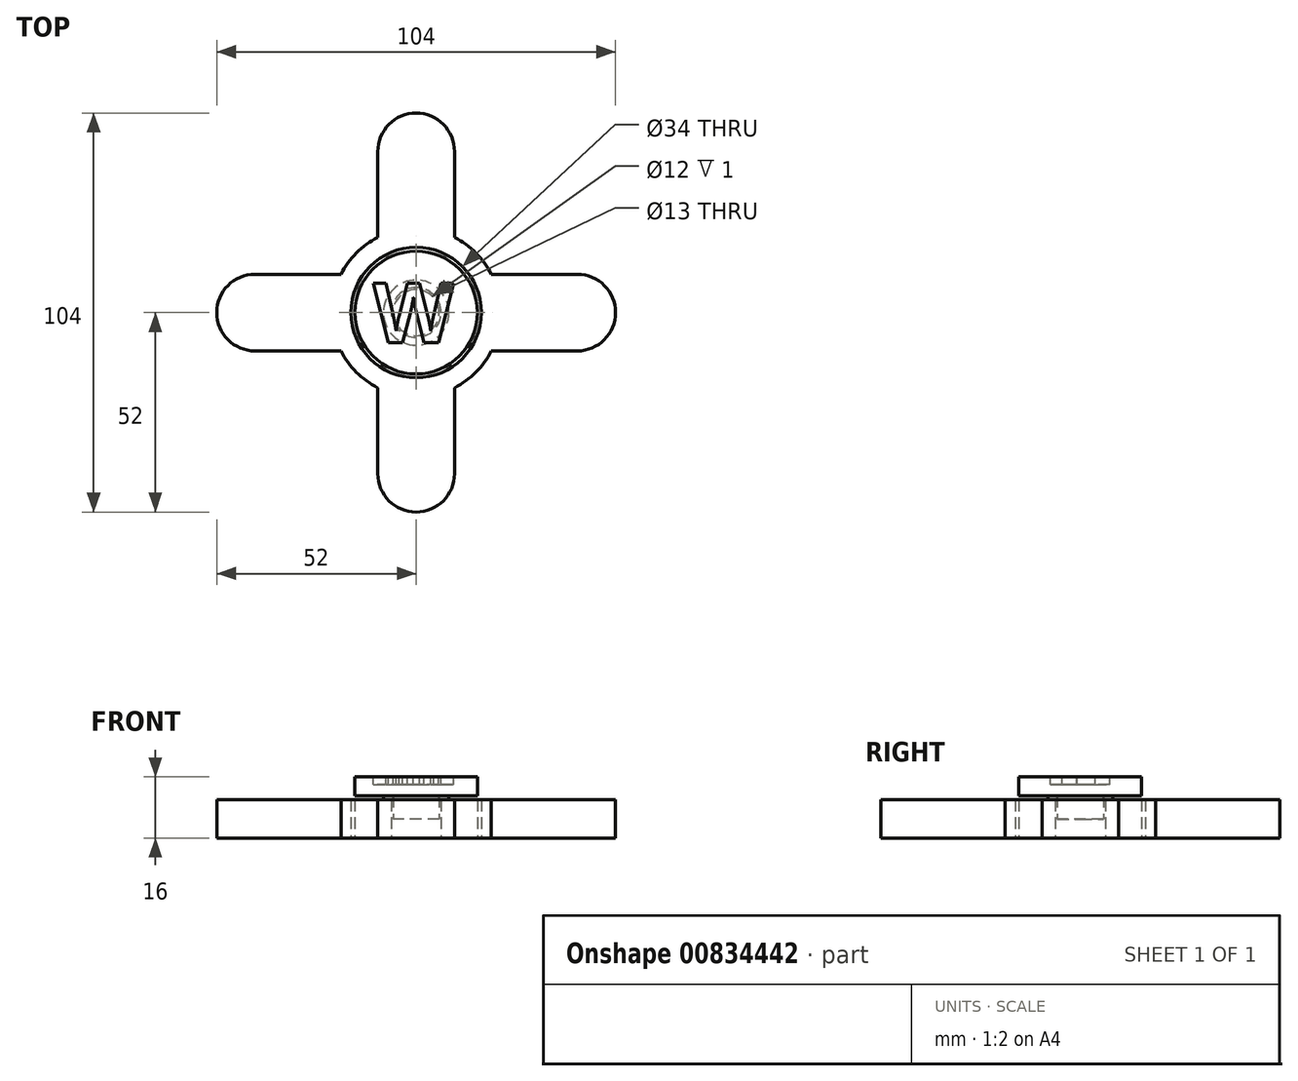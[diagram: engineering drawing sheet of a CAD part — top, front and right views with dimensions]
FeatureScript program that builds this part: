
annotation { "Feature Type Name" : "Feature", "Feature Type Description" : "" }
export const myFeature = defineFeature(function(context is Context, id is Id, definition is map)
    precondition{}
    {
        {
            var Q0;
            Q0=qCreatedBy(makeId("Top.planeOp"),FACE);
            var sketch = newSketch(context, id + "F0", { "sketchPlane" : qUnion([Q0])});
            skCircle(sketch, "E0", {"center": v(0, 0) * mm, "radius": 16 * mm});
            skCircle(sketch, "E1", {"center": v(0, 0) * mm, "radius": 6.5 * mm});
            skCircle(sketch, "E2", {"center": v(0, 0) * mm, "radius": 17 * mm});
            skCircle(sketch, "E3", {"center": v(0, 0) * mm, "radius": 22 * mm});
            skCircle(sketch, "E4", {"center": v(0, 0) * mm, "radius": 4.5 * mm});
            skPoint(sketch, "E5", {"position": v(0, -22) * mm});
            skLineSegment(sketch, "E6", {"start": v(-10, -19.6) * mm, "end": v(-10, -52) * mm});
            skLineSegment(sketch, "E7", {"start": v(-10, -52) * mm, "end": v(10, -52) * mm});
            skLineSegment(sketch, "E8", {"start": v(10, -52) * mm, "end": v(10, -19.6) * mm});
            skPoint(sketch, "E9", {"position": v(0, -52) * mm});
            skPoint(sketch, "E10", {"position": v(-22, 0) * mm});
            skPoint(sketch, "E11", {"position": v(22, 0) * mm});
            skPoint(sketch, "E12", {"position": v(0, 22) * mm});
            skLineSegment(sketch, "E13", {"start": v(-19.6, 10) * mm, "end": v(-52, 10) * mm});
            skLineSegment(sketch, "E14", {"start": v(-52, 10) * mm, "end": v(-52, -10) * mm});
            skLineSegment(sketch, "E15", {"start": v(-52, -10) * mm, "end": v(-19.6, -10) * mm});
            skPoint(sketch, "E16", {"position": v(-52, 0) * mm});
            skLineSegment(sketch, "E17", {"start": v(-10, 19.6) * mm, "end": v(-10, 52) * mm});
            skLineSegment(sketch, "E18", {"start": v(-10, 52) * mm, "end": v(10, 52) * mm});
            skLineSegment(sketch, "E19", {"start": v(10, 52) * mm, "end": v(10, 19.6) * mm});
            skPoint(sketch, "E20", {"position": v(0, 52) * mm});
            skLineSegment(sketch, "E21", {"start": v(19.6, -10) * mm, "end": v(52, -10) * mm});
            skLineSegment(sketch, "E22", {"start": v(52, -10) * mm, "end": v(52, 10) * mm});
            skLineSegment(sketch, "E23", {"start": v(52, 10) * mm, "end": v(19.6, 10) * mm});
            skPoint(sketch, "E24", {"position": v(52, 0) * mm});
            skSolve(sketch);
        }
        {
            var Q0;
            {var subQ0=sQuery(id+"F0.wireOp",EDGE,"gpfM4k37-eCNT-VDhr-O2bJ-2ocuH3XYZRLL");var subQ1=sQuery(id+"F0.wireOp",EDGE,"E2");var subQ2=makeQuery(id+"F0.imprint","INTERSECT",VERTEX,{"derivedFrom":[subQ1,subQ0]});Q0=makeQuery(id+"F0.imprint","IMPRINT",FACE,{"disambiguationData":[TD([[makeQuery(id+"F0.imprint","IMPRINT",EDGE,{"disambiguationData":[TD([[subQ2,1.0]])],"derivedFrom":subQ1}),-1.0]])]});}
            var Q1;
            {var subQ0=sQuery(id+"F0.wireOp",EDGE,"wSeqBDBI-Kv3G-UAp7-a8cB-W62R1kd8twcA");var subQ1=sQuery(id+"F0.wireOp",EDGE,"E2");var subQ2=makeQuery(id+"F0.imprint","INTERSECT",VERTEX,{"derivedFrom":[subQ1,subQ0]});Q1=makeQuery(id+"F0.imprint","IMPRINT",FACE,{"disambiguationData":[TD([[makeQuery(id+"F0.imprint","IMPRINT",EDGE,{"disambiguationData":[TD([[subQ2,1.0]])],"derivedFrom":subQ1}),-1.0]])]});}
            var Q2;
            {var subQ0=sQuery(id+"F0.wireOp",EDGE,"S2Hn9LyL-7IjH-aa6G-lDFo-Ye3rjhQq9e6S");var subQ1=sQuery(id+"F0.wireOp",EDGE,"E2");var subQ2=makeQuery(id+"F0.imprint","INTERSECT",VERTEX,{"derivedFrom":[subQ1,subQ0]});Q2=makeQuery(id+"F0.imprint","IMPRINT",FACE,{"disambiguationData":[TD([[makeQuery(id+"F0.imprint","IMPRINT",EDGE,{"disambiguationData":[TD([[subQ2,-1.0]])],"derivedFrom":subQ1}),-1.0]])]});}
            var Q3;
            Q3=makeQuery(id+"F0.imprint","IMPRINT",FACE,{"disambiguationData":[TD([[makeQuery(id+"F0.imprint","IMPRINT",EDGE,{"derivedFrom":sQuery(id+"F0.wireOp",EDGE,"E0")}),1.0]])]});
            var Q4;
            Q4=makeQuery(id+"F0.imprint","IMPRINT",FACE,{"disambiguationData":[TD([[makeQuery(id+"F0.imprint","IMPRINT",EDGE,{"derivedFrom":sQuery(id+"F0.wireOp",EDGE,"E3")}),-1.0]])]});
            extrude(context, id + "F1", {"entities" : qUnion([Q0, Q1, Q2, Q3, Q4]), "depth" : 10 * mm, "offsetDistance" : 25 * mm});
        }
        {
            var Q0;
            Q0=qCreatedBy(makeId("Top.planeOp"),FACE);
            cPlane(context, id + "F2", {"entities" : qUnion([Q0]), "cplaneType" : CPlaneType.OFFSET, "offset" : 5 * mm, "width" : 150 * mm, "height" : 150 * mm});
        }
        {
            var Q0;
            Q0=qCreatedBy(id+"F2.planeOp",FACE);
            var sketch = newSketch(context, id + "F3", { "sketchPlane" : qUnion([Q0])});
            skCircle(sketch, "E25.0", {"center": v(0, 0) * mm, "radius": 16 * mm});
            skCircle(sketch, "E26.0", {"center": v(0, 0) * mm, "radius": 17 * mm});
            skCircle(sketch, "E27.0", {"center": v(0, 0) * mm, "radius": 22 * mm});
            skCircle(sketch, "E28.0", {"center": v(0, 0) * mm, "radius": 6.5 * mm});
            skCircle(sketch, "E29", {"center": v(0, 0) * mm, "radius": 6 * mm});
            skSolve(sketch);
        }
        {
            var Q0;
            Q0=makeQuery(id+"F3.imprint","IMPRINT",FACE,{"disambiguationData":[TD([[makeQuery(id+"F3.imprint","IMPRINT",EDGE,{"derivedFrom":sQuery(id+"F3.wireOp",EDGE,"E29")}),1.0]])]});
            extrude(context, id + "F4", {"entities" : qUnion([Q0]), "depth" : 6 * mm, "offsetDistance" : 25 * mm});
        }
        {
            var Q0;
            Q0=makeQuery(id+"F4.opExtrude","CAP_FACE",FACE,{"disambiguationData":[OSD([sQuery(id+"F3.wireOp",EDGE,"E29")])],"isStart":false});
            var sketch = newSketch(context, id + "F5", { "sketchPlane" : qUnion([Q0])});
            skCircle(sketch, "E30.0", {"center": v(0, 0) * mm, "radius": 16 * mm});
            skSolve(sketch);
        }
        {
            var Q0;
            Q0=makeQuery(id+"F5.imprint","IMPRINT",FACE,{"disambiguationData":[TD([[makeQuery(id+"F5.imprint","IMPRINT",EDGE,{"derivedFrom":sQuery(id+"F5.wireOp",EDGE,"E30.0")}),1.0]])]});
            var Q1;
            Q1=makeQuery(id+"F5.imprint","IMPRINT",FACE,{"disambiguationData":[TD([[makeQuery(id+"F5.imprint","IMPRINT",EDGE,{"derivedFrom":makeQuery(id+"F4.opExtrude","CAP_EDGE",EDGE,{"disambiguationData":[OSD([sQuery(id+"F3.wireOp",EDGE,"E29")])],"isStart":false})}),1.0]])]});
            extrude(context, id + "F6", {"entities" : qUnion([Q0, Q1]), "depth" : 5 * mm, "offsetDistance" : 25 * mm});
        }
        {
            var Q0;
            Q0=makeQuery(id+"F6.opExtrude","CAP_FACE",FACE,{"disambiguationData":[OSD([sQuery(id+"F5.wireOp",EDGE,"E30.0")])],"isStart":false});
            var sketch = newSketch(context, id + "F7", { "sketchPlane" : qUnion([Q0])});
            skPoint(sketch, "E31", {"position": v(0, 0) * mm});
            skCircle(sketch, "E32.0", {"center": v(0, 0) * mm, "radius": 16 * mm});
            skPoint(sketch, "E33", {"position": v(16, 0) * mm});
            skText(sketch, "E34", { "text": "W", "fontName": "OpenSans-Bold.ttf"});
            const initialGuessF7  = {"E34": [-0.01114, -0.00778, 1, 0, 0.01555]};
            skSetInitialGuess(sketch, initialGuessF7);
            skSolve(sketch);
        }
        {
            var Q0;
            Q0=makeQuery(id+"F7.imprint","IMPRINT",FACE,{"disambiguationData":[TD([[makeQuery(id+"F7.imprint","IMPRINT",EDGE,{"derivedFrom":sQuery(id+"F7.wireOp",EDGE,"E34.sketch_text.stroke-0")}),-1.0]])]});
            extrude(context, id + "F8", {"entities" : qUnion([Q0]), "operationType" : NewBodyOperationType.REMOVE, "oppositeDirection" : true, "depth" : 2 * mm, "offsetDistance" : 25 * mm});
        }
        {
            var Q0;
            Q0=makeQuery(id+"F1.opExtrude","SWEPT_EDGE",EDGE,{"disambiguationData":[OSD([sQuery(id+"F0.wireOp",EDGE,"E14"),sQuery(id+"F0.wireOp",EDGE,"E15")])]});
            var Q1;
            Q1=makeQuery(id+"F1.opExtrude","SWEPT_EDGE",EDGE,{"disambiguationData":[OSD([sQuery(id+"F0.wireOp",EDGE,"E13"),sQuery(id+"F0.wireOp",EDGE,"E14")])]});
            var Q2;
            Q2=makeQuery(id+"F1.opExtrude","SWEPT_EDGE",EDGE,{"disambiguationData":[OSD([sQuery(id+"F0.wireOp",EDGE,"E17"),sQuery(id+"F0.wireOp",EDGE,"E18")])]});
            var Q3;
            Q3=makeQuery(id+"F1.opExtrude","SWEPT_EDGE",EDGE,{"disambiguationData":[OSD([sQuery(id+"F0.wireOp",EDGE,"E18"),sQuery(id+"F0.wireOp",EDGE,"E19")])]});
            var Q4;
            Q4=makeQuery(id+"F1.opExtrude","SWEPT_EDGE",EDGE,{"disambiguationData":[OSD([sQuery(id+"F0.wireOp",EDGE,"E22"),sQuery(id+"F0.wireOp",EDGE,"E23")])]});
            var Q5;
            Q5=makeQuery(id+"F1.opExtrude","SWEPT_EDGE",EDGE,{"disambiguationData":[OSD([sQuery(id+"F0.wireOp",EDGE,"E21"),sQuery(id+"F0.wireOp",EDGE,"E22")])]});
            var Q6;
            Q6=makeQuery(id+"F1.opExtrude","SWEPT_EDGE",EDGE,{"disambiguationData":[OSD([sQuery(id+"F0.wireOp",EDGE,"E7"),sQuery(id+"F0.wireOp",EDGE,"E8")])]});
            var Q7;
            Q7=makeQuery(id+"F1.opExtrude","SWEPT_EDGE",EDGE,{"disambiguationData":[OSD([sQuery(id+"F0.wireOp",EDGE,"E6"),sQuery(id+"F0.wireOp",EDGE,"E7")])]});
            fillet(context, id + "F9", {"entities" : qUnion([Q0, Q1, Q2, Q3, Q4, Q5, Q6, Q7]), "radius" : 10 * mm, "tangentPropagation" : true, "allowEdgeOverflow" : false});
        }
        {
            var Q0;
            Q0=makeQuery(id+"F6.opExtrude","CAP_FACE",FACE,{"disambiguationData":[OSD([sQuery(id+"F5.wireOp",EDGE,"E30.0")])],"isStart":true});
            var sketch = newSketch(context, id + "F10", { "sketchPlane" : qUnion([Q0])});
            skCircle(sketch, "E35.0", {"center": v(0, 0) * mm, "radius": 6 * mm});
            skCircle(sketch, "E36", {"center": v(0, 0) * mm, "radius": 8.5 * mm});
            skSolve(sketch);
        }
        {
            var Q0;
            Q0=makeQuery(id+"F10.imprint","IMPRINT",FACE,{"disambiguationData":[TD([[makeQuery(id+"F10.imprint","IMPRINT",EDGE,{"derivedFrom":sQuery(id+"F10.wireOp",EDGE,"E35.0")}),-1.0]])]});
            extrude(context, id + "F11", {"entities" : qUnion([Q0]), "depth" : 1 * mm, "offsetDistance" : 25 * mm});
        }
    });
